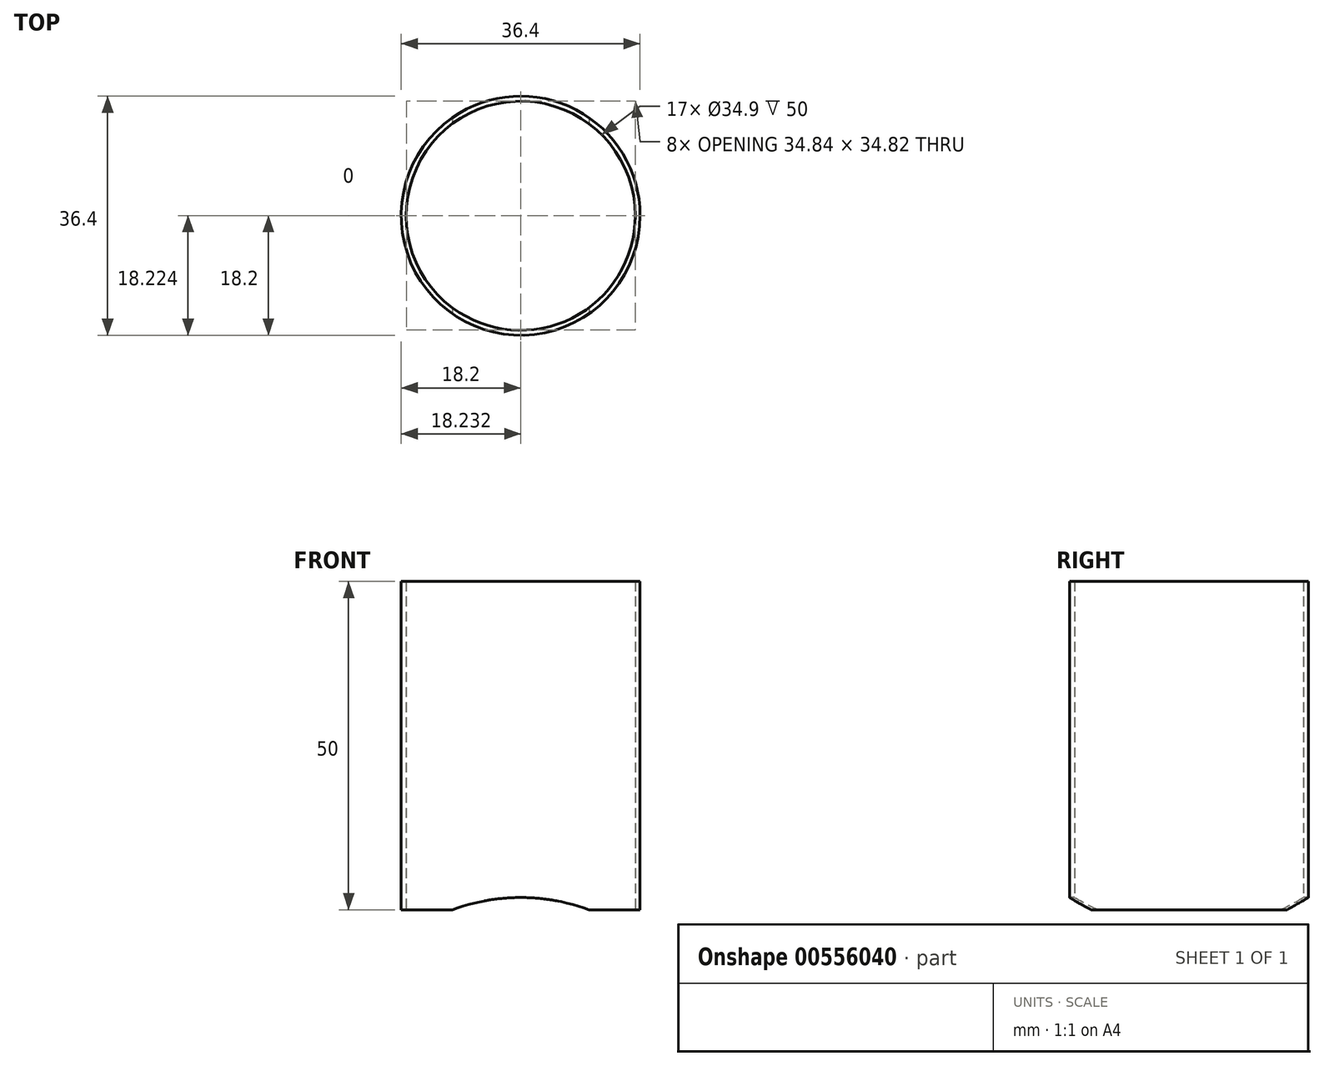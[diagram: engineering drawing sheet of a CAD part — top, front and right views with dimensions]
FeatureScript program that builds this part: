
annotation { "Feature Type Name" : "Feature", "Feature Type Description" : "" }
export const myFeature = defineFeature(function(context is Context, id is Id, definition is map)
    precondition{}
    {
        {
            var Q0;
            Q0=qCreatedBy(makeId("Top.planeOp"),FACE);
            var sketch = newSketch(context, id + "F0", { "sketchPlane" : qUnion([Q0])});
            skCircle(sketch, "E0", {"center": v(0, 0) * mm, "radius": 17.45 * mm});
            skCircle(sketch, "E1", {"center": v(0, 0) * mm, "radius": 18.2 * mm});
            skSolve(sketch);
        }
        {
            var Q0;
            Q0=makeQuery(id+"F0.imprint","IMPRINT",FACE,{"disambiguationData":[TD([[makeQuery(id+"F0.imprint","IMPRINT",EDGE,{"derivedFrom":sQuery(id+"F0.wireOp",EDGE,"E0")}),-1.0]])]});
            extrude(context, id + "F1", {"entities" : qUnion([Q0]), "depth" : 50 * mm, "offsetDistance" : 25 * mm});
        }
        {
            var Q0;
            Q0=qCreatedBy(makeId("Front.planeOp"),FACE);
            var sketch = newSketch(context, id + "F2", { "sketchPlane" : qUnion([Q0])});
            skLineSegment(sketch, "E2", {"start": v(-10.4, 0) * mm, "end": v(10.4, 0) * mm});
            skArc(sketch, "E3", {"start": v(10.4, 0) * mm, "mid": v(0, 1.86) * mm, "end": v(-10.4, 0) * mm});
            skSolve(sketch);
        }
        {
            var Q0;
            Q0=makeQuery(id+"F2.imprint","IMPRINT",FACE,{"disambiguationData":[TD([[makeQuery(id+"F2.imprint","IMPRINT",EDGE,{"derivedFrom":sQuery(id+"F2.wireOp",EDGE,"E2")}),1.0]])]});
            var Q1;
            Q1=sQuery(id+"F2.wireOp",EDGE,"E2");
            var Q2;
            Q2=sQuery(id+"F2.wireOp",EDGE,"E3");
            extrude(context, id + "F3", {"entities" : qUnion([Q0]), "operationType" : NewBodyOperationType.REMOVE, "surfaceEntities" : qUnion([Q1, Q2]), "endBound" : BoundingType.SYMMETRIC, "oppositeDirection" : true, "depth" : 190 * mm, "offsetDistance" : 25 * mm});
        }
    });
